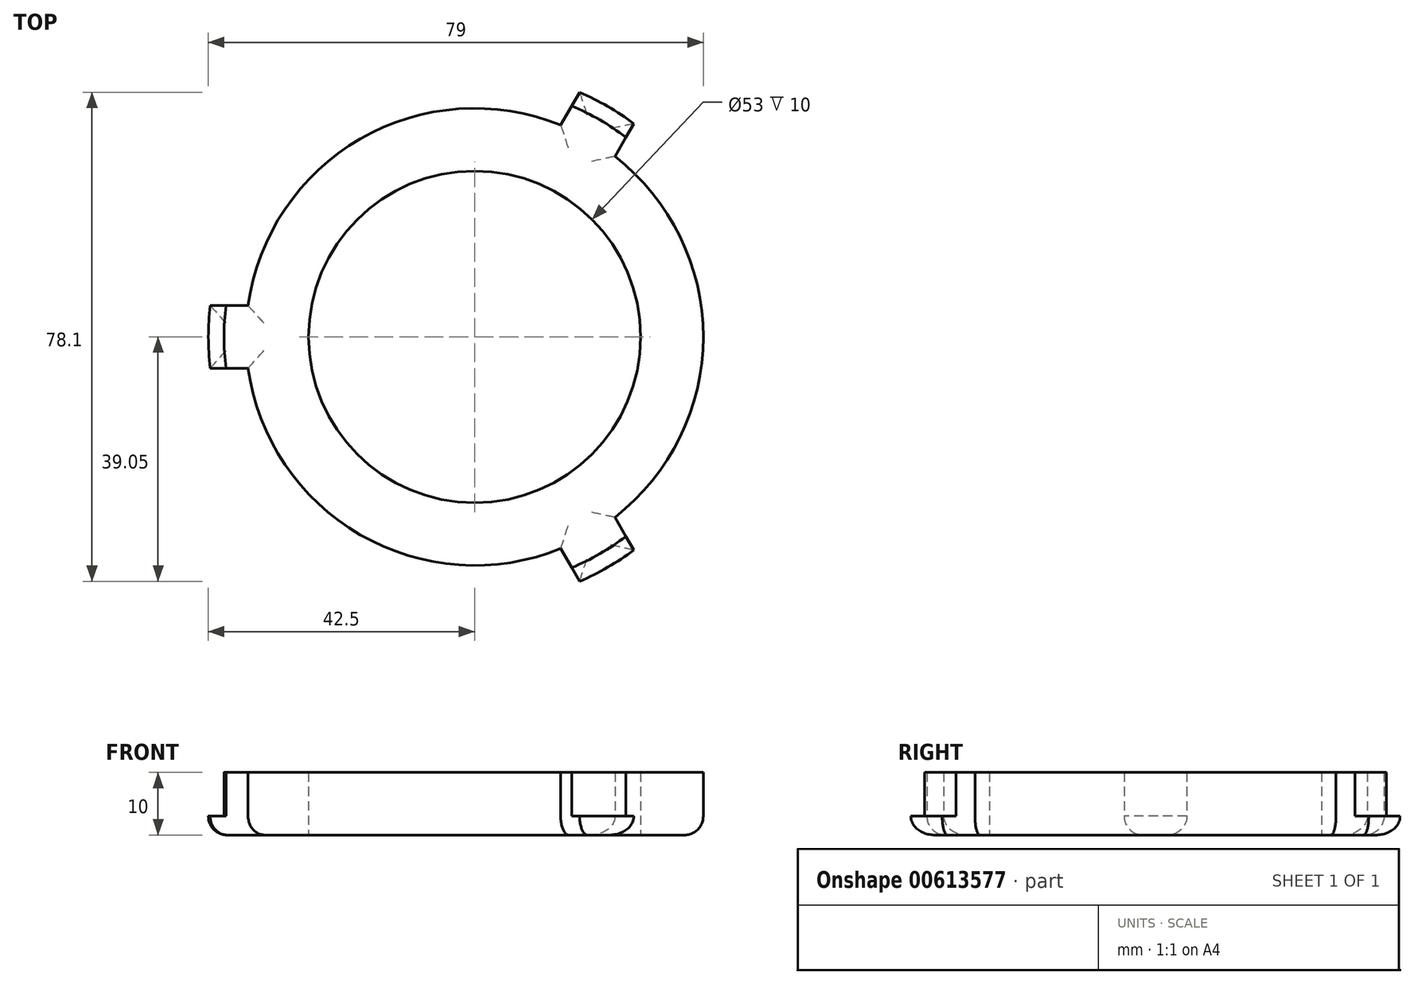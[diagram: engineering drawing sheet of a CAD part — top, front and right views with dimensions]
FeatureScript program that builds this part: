
annotation { "Feature Type Name" : "Feature", "Feature Type Description" : "" }
export const myFeature = defineFeature(function(context is Context, id is Id, definition is map)
    precondition{}
    {
        {
            var Q0;
            Q0=qCreatedBy(makeId("Top.planeOp"),FACE);
            var sketch = newSketch(context, id + "F0", { "sketchPlane" : qUnion([Q0])});
            skArc(sketch, "E0", {"start": v(-42.2, 5) * mm, "mid": v(-42.5, 0) * mm, "end": v(-42.2, -5) * mm});
            skArc(sketch, "E1", {"start": v(-39.69, 5) * mm, "mid": v(-40, 0) * mm, "end": v(-39.69, -5) * mm});
            skCircle(sketch, "E2", {"center": v(0, 0) * mm, "radius": 26.5 * mm});
            skCircle(sketch, "E3", {"center": v(0, 0) * mm, "radius": 36.5 * mm});
            skLineSegment(sketch, "E4", {"start": v(-42.2, 5) * mm, "end": v(-36.16, 5) * mm});
            skLineSegment(sketch, "E5", {"start": v(-42.2, -5) * mm, "end": v(-36.16, -5) * mm});
            skLineSegment(sketch, "E6", {"start": v(13.75, 33.81) * mm, "end": v(16.77, 39.05) * mm});
            skLineSegment(sketch, "E7", {"start": v(22.4, 28.81) * mm, "end": v(25.43, 34.05) * mm});
            skLineSegment(sketch, "E8", {"start": v(22.4, -28.81) * mm, "end": v(25.43, -34.05) * mm});
            skLineSegment(sketch, "E9", {"start": v(13.75, -33.81) * mm, "end": v(16.77, -39.05) * mm});
            skArc(sketch, "E10.trimOffspring", {"start": v(25.43, 34.05) * mm, "mid": v(21.25, 36.8) * mm, "end": v(16.77, 39.05) * mm});
            skArc(sketch, "E11.trimOffspring", {"start": v(24.17, 31.87) * mm, "mid": v(20, 34.64) * mm, "end": v(15.51, 36.87) * mm});
            skArc(sketch, "E12.trimOffspring", {"start": v(15.51, -36.87) * mm, "mid": v(20, -34.64) * mm, "end": v(24.17, -31.87) * mm});
            skArc(sketch, "E13.trimOffspring", {"start": v(16.77, -39.05) * mm, "mid": v(21.25, -36.8) * mm, "end": v(25.43, -34.05) * mm});
            skSolve(sketch);
        }
        {
            var Q0;
            {var subQ0=sQuery(id+"F0.wireOp",EDGE,"E0");Q0=makeQuery(id+"F0.imprint","IMPRINT",FACE,{"disambiguationData":[TD([[makeQuery(id+"F0.imprint","IMPRINT",EDGE,{"derivedFrom":subQ0}),1.0]])]});}
            var Q1;
            Q1=makeQuery(id+"F0.imprint","IMPRINT",FACE,{"disambiguationData":[TD([[makeQuery(id+"F0.imprint","IMPRINT",EDGE,{"derivedFrom":sQuery(id+"F0.wireOp",EDGE,"E2")}),-1.0]])]});
            var Q2;
            {var subQ0=sQuery(id+"F0.wireOp",EDGE,"E1");Q2=makeQuery(id+"F0.imprint","IMPRINT",FACE,{"disambiguationData":[TD([[makeQuery(id+"F0.imprint","IMPRINT",EDGE,{"derivedFrom":subQ0}),1.0]])]});}
            var Q3;
            {var subQ2=sQuery(id+"F0.wireOp",EDGE,"E12.trimOffspring");Q3=makeQuery(id+"F0.imprint","IMPRINT",FACE,{"disambiguationData":[TD([[makeQuery(id+"F0.imprint","IMPRINT",EDGE,{"derivedFrom":subQ2}),-1.0]])]});}
            var Q4;
            {var subQ5=sQuery(id+"F0.wireOp",EDGE,"E11.trimOffspring");Q4=makeQuery(id+"F0.imprint","IMPRINT",FACE,{"disambiguationData":[TD([[makeQuery(id+"F0.imprint","IMPRINT",EDGE,{"derivedFrom":subQ5}),1.0]])]});}
            var Q5;
            {var subQ0=sQuery(id+"F0.wireOp",EDGE,"E10.trimOffspring");Q5=makeQuery(id+"F0.imprint","IMPRINT",FACE,{"disambiguationData":[TD([[makeQuery(id+"F0.imprint","IMPRINT",EDGE,{"derivedFrom":subQ0}),1.0]])]});}
            var Q6;
            {var subQ5=sQuery(id+"F0.wireOp",EDGE,"E12.trimOffspring");Q6=makeQuery(id+"F0.imprint","IMPRINT",FACE,{"disambiguationData":[TD([[makeQuery(id+"F0.imprint","IMPRINT",EDGE,{"derivedFrom":subQ5}),1.0]])]});}
            extrude(context, id + "F1", {"entities" : qUnion([Q0, Q1, Q2, Q3, Q4, Q5, Q6]), "depth" : 3 * mm, "offsetDistance" : 25 * mm});
        }
        {
            var Q0;
            {var subQ5=sQuery(id+"F0.wireOp",EDGE,"E11.trimOffspring");Q0=makeQuery(id+"F0.imprint","IMPRINT",FACE,{"disambiguationData":[TD([[makeQuery(id+"F0.imprint","IMPRINT",EDGE,{"derivedFrom":subQ5}),1.0]])]});}
            var Q1;
            Q1=makeQuery(id+"F0.imprint","IMPRINT",FACE,{"disambiguationData":[TD([[makeQuery(id+"F0.imprint","IMPRINT",EDGE,{"derivedFrom":sQuery(id+"F0.wireOp",EDGE,"E2")}),-1.0]])]});
            var Q2;
            {var subQ0=sQuery(id+"F0.wireOp",EDGE,"E1");Q2=makeQuery(id+"F0.imprint","IMPRINT",FACE,{"disambiguationData":[TD([[makeQuery(id+"F0.imprint","IMPRINT",EDGE,{"derivedFrom":subQ0}),1.0]])]});}
            var Q3;
            {var subQ5=sQuery(id+"F0.wireOp",EDGE,"E12.trimOffspring");Q3=makeQuery(id+"F0.imprint","IMPRINT",FACE,{"disambiguationData":[TD([[makeQuery(id+"F0.imprint","IMPRINT",EDGE,{"derivedFrom":subQ5}),1.0]])]});}
            extrude(context, id + "F2", {"entities" : qUnion([Q0, Q1, Q2, Q3]), "operationType" : NewBodyOperationType.ADD, "depth" : 10 * mm, "offsetDistance" : 25 * mm});
        }
        {
            var Q0;
            Q0=makeQuery(id+"F1.opExtrude","CAP_EDGE",EDGE,{"disambiguationData":[OSD([sQuery(id+"F0.wireOp",EDGE,"E0")])],"isStart":true});
            var Q1;
            {var subQ0=sQuery(id+"F0.wireOp",EDGE,"E3");Q1=makeQuery(id+"F1.opExtrude","CAP_EDGE",EDGE,{"disambiguationData":[OSD([subQ0]),TDD([makeQuery(id+"F0.imprint","IMPRINT",EDGE,{"disambiguationData":[TD([[makeQuery(id+"F0.imprint","INTERSECT",VERTEX,{"derivedFrom":[subQ0,sQuery(id+"F0.wireOp",EDGE,"E5")]}),-1.0]])],"derivedFrom":subQ0})])],"isStart":true});}
            var Q2;
            Q2=makeQuery(id+"F1.opExtrude","CAP_EDGE",EDGE,{"disambiguationData":[OSD([sQuery(id+"F0.wireOp",EDGE,"E13.trimOffspring")])],"isStart":true});
            var Q3;
            {var subQ0=sQuery(id+"F0.wireOp",EDGE,"E3");Q3=makeQuery(id+"F1.opExtrude","CAP_EDGE",EDGE,{"disambiguationData":[OSD([subQ0]),TDD([makeQuery(id+"F0.imprint","IMPRINT",EDGE,{"disambiguationData":[TD([[makeQuery(id+"F0.imprint","INTERSECT",VERTEX,{"derivedFrom":[subQ0,sQuery(id+"F0.wireOp",EDGE,"E7")]}),1.0]])],"derivedFrom":subQ0})])],"isStart":true});}
            var Q4;
            Q4=makeQuery(id+"F1.opExtrude","CAP_EDGE",EDGE,{"disambiguationData":[OSD([sQuery(id+"F0.wireOp",EDGE,"E10.trimOffspring")])],"isStart":true});
            var Q5;
            {var subQ0=sQuery(id+"F0.wireOp",EDGE,"E3");Q5=makeQuery(id+"F1.opExtrude","CAP_EDGE",EDGE,{"disambiguationData":[OSD([subQ0]),TDD([makeQuery(id+"F0.imprint","IMPRINT",EDGE,{"disambiguationData":[TD([[makeQuery(id+"F0.imprint","INTERSECT",VERTEX,{"derivedFrom":[subQ0,sQuery(id+"F0.wireOp",EDGE,"E4")]}),1.0]])],"derivedFrom":subQ0})])],"isStart":true});}
            var Q6;
            Q6=makeQuery(id+"F1.opExtrude","CAP_EDGE",EDGE,{"disambiguationData":[OSD([sQuery(id+"F0.wireOp",EDGE,"E4")])],"isStart":true});
            var Q7;
            Q7=makeQuery(id+"F1.opExtrude","CAP_EDGE",EDGE,{"disambiguationData":[OSD([sQuery(id+"F0.wireOp",EDGE,"E6")])],"isStart":true});
            var Q8;
            Q8=makeQuery(id+"F1.opExtrude","CAP_EDGE",EDGE,{"disambiguationData":[OSD([sQuery(id+"F0.wireOp",EDGE,"E7")])],"isStart":true});
            var Q9;
            Q9=makeQuery(id+"F1.opExtrude","CAP_EDGE",EDGE,{"disambiguationData":[OSD([sQuery(id+"F0.wireOp",EDGE,"E8")])],"isStart":true});
            var Q10;
            Q10=makeQuery(id+"F1.opExtrude","CAP_EDGE",EDGE,{"disambiguationData":[OSD([sQuery(id+"F0.wireOp",EDGE,"E9")])],"isStart":true});
            var Q11;
            Q11=makeQuery(id+"F1.opExtrude","CAP_EDGE",EDGE,{"disambiguationData":[OSD([sQuery(id+"F0.wireOp",EDGE,"E5")])],"isStart":true});
            fillet(context, id + "F3", {"entities" : qUnion([Q0, Q1, Q2, Q3, Q4, Q5, Q6, Q7, Q8, Q9, Q10, Q11]), "radius" : 3 * mm, "tangentPropagation" : true, "allowEdgeOverflow" : false});
        }
    });
